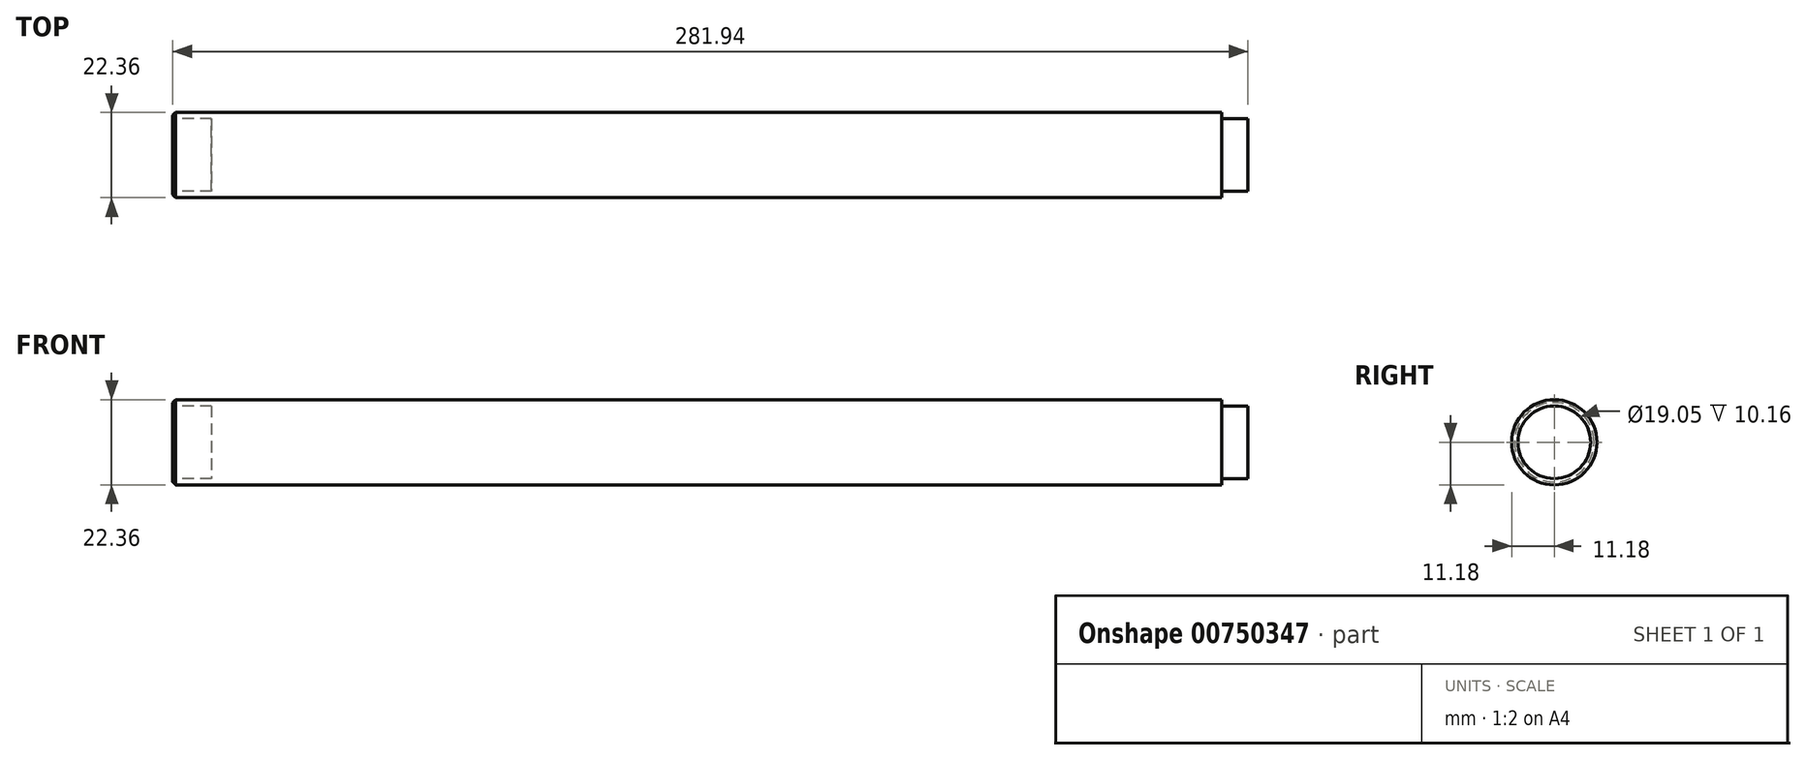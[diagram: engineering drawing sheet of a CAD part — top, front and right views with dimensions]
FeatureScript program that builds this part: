
annotation { "Feature Type Name" : "Feature", "Feature Type Description" : "" }
export const myFeature = defineFeature(function(context is Context, id is Id, definition is map)
    precondition{}
    {
        {
            var Q0;
            Q0=qCreatedBy(makeId("Right.planeOp"),FACE);
            var sketch = newSketch(context, id + "F0", { "sketchPlane" : qUnion([Q0])});
            skCircle(sketch, "E0", {"center": v(0, 0) * mm, "radius": 11.18 * mm});
            skSolve(sketch);
        }
        {
            var Q0;
            Q0 = qSketchRegion(id + "F0", true);
            extrude(context, id + "F1", {"entities" : qUnion([Q0]), "endBound" : BoundingType.SYMMETRIC, "depth" : 281.94 * mm, "offsetDistance" : 25.4 * mm});
        }
        {
            var Q0;
            Q0=makeQuery(id+"F1.opExtrude","CAP_FACE",FACE,{"disambiguationData":[OSD([sQuery(id+"F0.wireOp",EDGE,"E0")])],"isStart":false});
            var sketch = newSketch(context, id + "F2", { "sketchPlane" : qUnion([Q0])});
            skCircle(sketch, "E1", {"center": v(0, 0) * mm, "radius": 9.53 * mm});
            skCircle(sketch, "E2", {"center": v(0, 0) * mm, "radius": 11.18 * mm});
            skSolve(sketch);
        }
        {
            var Q0;
            Q0=makeQuery(id+"F2.imprint","IMPRINT",FACE,{"disambiguationData":[TD([[makeQuery(id+"F2.imprint","IMPRINT",EDGE,{"derivedFrom":sQuery(id+"F2.wireOp",EDGE,"E1")}),-1.0]])]});
            extrude(context, id + "F3", {"entities" : qUnion([Q0]), "operationType" : NewBodyOperationType.REMOVE, "oppositeDirection" : true, "depth" : 6.86 * mm, "offsetDistance" : 25.4 * mm});
        }
        {
            var Q0;
            Q0=makeQuery(id+"F1.opExtrude","CAP_EDGE",EDGE,{"disambiguationData":[OSD([sQuery(id+"F0.wireOp",EDGE,"E0")])],"isStart":true});
            var Q1;
            Q1=makeQuery(id+"F3.boolean.opBoolean","COPY",EDGE,{"derivedFrom":makeQuery(id+"F3.opExtrude","CAP_EDGE",EDGE,{"disambiguationData":[OSD([sQuery(id+"F2.wireOp",EDGE,"E2")])],"isStart":false})});
            chamfer(context, id + "F4", {"entities" : qUnion([Q0, Q1]), "width" : 0.76 * mm, "tangentPropagation" : true});
        }
        {
            var Q0;
            Q0=makeQuery(id+"F1.opExtrude","CAP_FACE",FACE,{"disambiguationData":[OSD([sQuery(id+"F0.wireOp",EDGE,"E0")])],"isStart":true});
            var sketch = newSketch(context, id + "F5", { "sketchPlane" : qUnion([Q0])});
            skCircle(sketch, "E3", {"center": v(0, 0) * mm, "radius": 9.53 * mm});
            skSolve(sketch);
        }
        {
            var Q0;
            Q0 = qSketchRegion(id + "F5", true);
            extrude(context, id + "F6", {"entities" : qUnion([Q0]), "operationType" : NewBodyOperationType.REMOVE, "oppositeDirection" : true, "depth" : 10.16 * mm, "offsetDistance" : 25.4 * mm});
        }
    });
